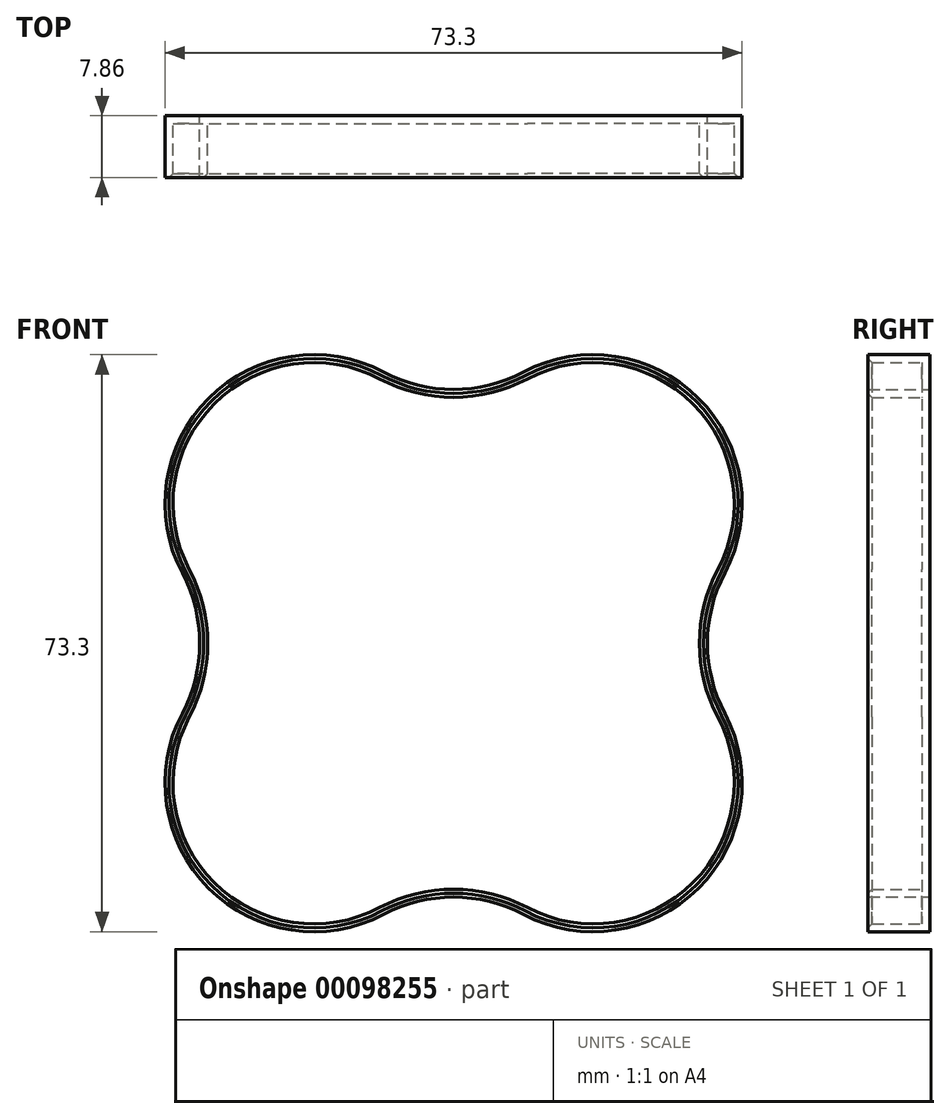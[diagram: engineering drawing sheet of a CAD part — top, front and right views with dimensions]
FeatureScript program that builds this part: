
annotation { "Feature Type Name" : "Feature", "Feature Type Description" : "" }
export const myFeature = defineFeature(function(context is Context, id is Id, definition is map)
    precondition{}
    {
        {
            var Q0;
            Q0=qCreatedBy(makeId("Front.planeOp"),FACE);
            var sketch = newSketch(context, id + "F0", { "sketchPlane" : qUnion([Q0])});
            skLineSegment(sketch, "E0.bottom", {"start": v(17.75, 17.75) * mm, "end": v(-17.75, 17.75) * mm, "construction": true});
            skLineSegment(sketch, "E0.top", {"start": v(17.75, -17.75) * mm, "end": v(-17.75, -17.75) * mm, "construction": true});
            skLineSegment(sketch, "E0.left", {"start": v(17.75, 17.75) * mm, "end": v(17.75, -17.75) * mm, "construction": true});
            skLineSegment(sketch, "E0.right", {"start": v(-17.75, 17.75) * mm, "end": v(-17.75, -17.75) * mm, "construction": true});
            skPoint(sketch, "E0.middle", {"position": v(0, 0) * mm});
            skArc(sketch, "E1", {"start": v(-34.46, 8.91) * mm, "mid": v(-31.11, 31.11) * mm, "end": v(-8.91, 34.46) * mm});
            skArc(sketch, "E2", {"start": v(8.91, 34.46) * mm, "mid": v(31.11, 31.11) * mm, "end": v(34.46, 8.91) * mm});
            skArc(sketch, "E3", {"start": v(34.46, -8.91) * mm, "mid": v(31.11, -31.11) * mm, "end": v(8.91, -34.46) * mm});
            skArc(sketch, "E4", {"start": v(-34.46, -8.91) * mm, "mid": v(-31.11, -31.11) * mm, "end": v(-8.91, -34.46) * mm});
            skArc(sketch, "E5", {"start": v(-34.46, 8.91) * mm, "mid": v(-32.24, 0) * mm, "end": v(-34.46, -8.91) * mm});
            skArc(sketch, "E6", {"start": v(-8.91, -34.46) * mm, "mid": v(0, -32.24) * mm, "end": v(8.91, -34.46) * mm});
            skArc(sketch, "E7", {"start": v(34.46, -8.91) * mm, "mid": v(32.24, 0) * mm, "end": v(34.46, 8.91) * mm});
            skArc(sketch, "E8", {"start": v(-8.91, 34.46) * mm, "mid": v(0, 32.24) * mm, "end": v(8.91, 34.46) * mm});
            skSolve(sketch);
        }
        {
            var Q0;
            Q0 = qSketchRegion(id + "F0", true);
            extrude(context, id + "F1", {"entities" : qUnion([Q0]), "depth" : 1 * mm});
        }
        {
            var Q0;
            Q0=makeQuery(id+"F1.opExtrude","CAP_FACE",FACE,{"disambiguationData":[OSD([sQuery(id+"F0.wireOp",EDGE,"E1"),sQuery(id+"F0.wireOp",EDGE,"E2"),sQuery(id+"F0.wireOp",EDGE,"E3"),sQuery(id+"F0.wireOp",EDGE,"E4"),sQuery(id+"F0.wireOp",EDGE,"E5"),sQuery(id+"F0.wireOp",EDGE,"E6"),sQuery(id+"F0.wireOp",EDGE,"E7"),sQuery(id+"F0.wireOp",EDGE,"E8")])],"isStart":false});
            var sketch = newSketch(context, id + "F2", { "sketchPlane" : qUnion([Q0])});
            skArc(sketch, "E9", {"start": v(-34.46, 8.91) * mm, "mid": v(-31.11, 31.11) * mm, "end": v(-8.91, 34.46) * mm});
            skArc(sketch, "E10", {"start": v(8.91, 34.46) * mm, "mid": v(31.11, 31.11) * mm, "end": v(34.46, 8.91) * mm});
            skArc(sketch, "E11", {"start": v(34.46, -8.91) * mm, "mid": v(31.11, -31.11) * mm, "end": v(8.91, -34.46) * mm});
            skArc(sketch, "E12", {"start": v(-8.91, -34.46) * mm, "mid": v(-31.11, -31.11) * mm, "end": v(-34.46, -8.91) * mm});
            skArc(sketch, "E13", {"start": v(-34.46, 8.91) * mm, "mid": v(-32.24, 0) * mm, "end": v(-34.46, -8.91) * mm});
            skArc(sketch, "E14", {"start": v(-8.91, -34.46) * mm, "mid": v(0, -32.24) * mm, "end": v(8.91, -34.46) * mm});
            skArc(sketch, "E15", {"start": v(34.46, -8.91) * mm, "mid": v(32.24, 0) * mm, "end": v(34.46, 8.91) * mm});
            skArc(sketch, "E16", {"start": v(8.91, 34.46) * mm, "mid": v(0, 32.24) * mm, "end": v(-8.91, 34.46) * mm});
            skArc(sketch, "E17.0", {"start": v(-33.57, 9.38) * mm, "mid": v(-31.24, 0) * mm, "end": v(-33.57, -9.38) * mm});
            skArc(sketch, "E17.1", {"start": v(-9.38, -33.57) * mm, "mid": v(-30.4, -30.4) * mm, "end": v(-33.57, -9.38) * mm});
            skArc(sketch, "E17.2", {"start": v(-33.57, 9.38) * mm, "mid": v(-30.4, 30.4) * mm, "end": v(-9.38, 33.57) * mm});
            skArc(sketch, "E17.3", {"start": v(-9.38, -33.57) * mm, "mid": v(0, -31.24) * mm, "end": v(9.38, -33.57) * mm});
            skArc(sketch, "E17.4", {"start": v(9.38, 33.57) * mm, "mid": v(0, 31.24) * mm, "end": v(-9.38, 33.57) * mm});
            skArc(sketch, "E17.5", {"start": v(9.38, 33.57) * mm, "mid": v(30.4, 30.4) * mm, "end": v(33.57, 9.38) * mm});
            skArc(sketch, "E17.6", {"start": v(33.57, -9.38) * mm, "mid": v(31.24, 0) * mm, "end": v(33.57, 9.38) * mm});
            skArc(sketch, "E17.7", {"start": v(33.57, -9.38) * mm, "mid": v(30.4, -30.4) * mm, "end": v(9.38, -33.57) * mm});
            skSolve(sketch);
        }
        {
            var Q0;
            Q0 = qSketchRegion(id + "F2", true);
            extrude(context, id + "F3", {"entities" : qUnion([Q0]), "operationType" : NewBodyOperationType.ADD, "depth" : 6.86 * mm});
        }
        {
            var Q0;
            Q0=makeQuery(id+"F3.opExtrude","CAP_EDGE",EDGE,{"disambiguationData":[OSD([sQuery(id+"F2.wireOp",EDGE,"E17.2")])],"isStart":false});
            chamfer(context, id + "F4", {"entities" : qUnion([Q0]), "width" : 0.5 * mm, "tangentPropagation" : true});
        }
    });
